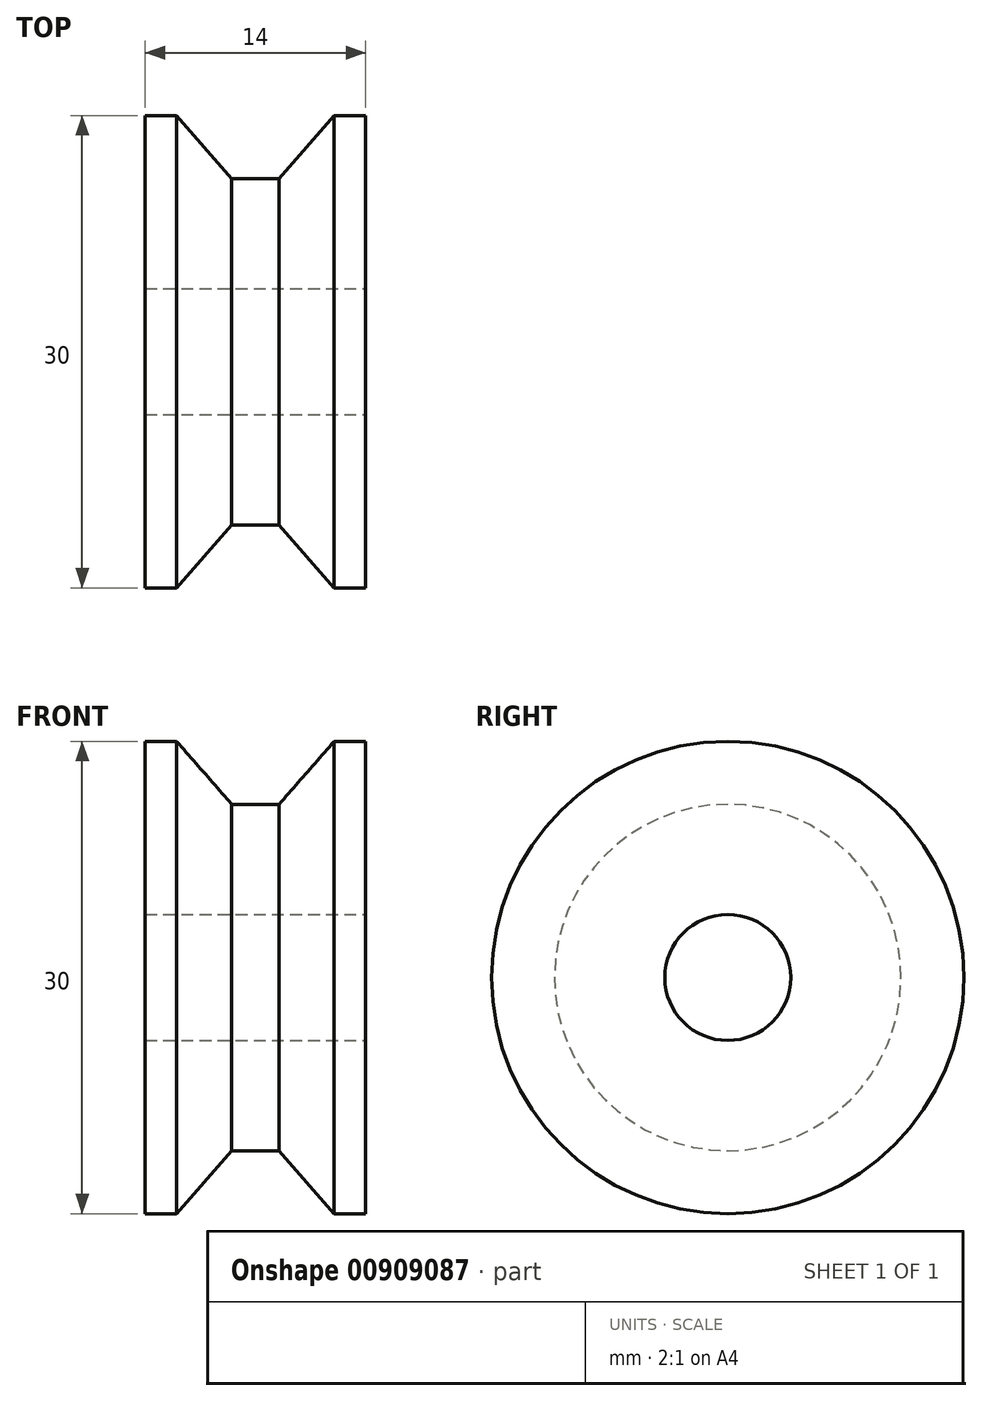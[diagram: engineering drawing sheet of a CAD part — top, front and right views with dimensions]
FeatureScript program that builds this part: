
annotation { "Feature Type Name" : "Feature", "Feature Type Description" : "" }
export const myFeature = defineFeature(function(context is Context, id is Id, definition is map)
    precondition{}
    {
        {
            var Q0;
            Q0=qCreatedBy(makeId("Front.planeOp"),FACE);
            var sketch = newSketch(context, id + "F0", { "sketchPlane" : qUnion([Q0])});
            skLineSegment(sketch, "E0", {"start": v(0, 0) * mm, "end": v(-7, 0) * mm});
            skLineSegment(sketch, "E1", {"start": v(-7, 0) * mm, "end": v(-7, 15) * mm});
            skLineSegment(sketch, "E2", {"start": v(-7, 15) * mm, "end": v(-5, 15) * mm});
            skLineSegment(sketch, "E3", {"start": v(-5, 15) * mm, "end": v(-1.5, 11) * mm});
            skLineSegment(sketch, "E4", {"start": v(-1.5, 11) * mm, "end": v(0, 11) * mm});
            skLineSegment(sketch, "E5", {"start": v(0, 11) * mm, "end": v(0, 0) * mm});
            skLineSegment(sketch, "E6.MirrorCS", {"start": v(0, 0) * mm, "end": v(7, 0) * mm});
            skLineSegment(sketch, "E7.MirrorCS", {"start": v(7, 0) * mm, "end": v(7, 15) * mm});
            skLineSegment(sketch, "E8.MirrorCS", {"start": v(7, 15) * mm, "end": v(5, 15) * mm});
            skLineSegment(sketch, "E9.MirrorCS", {"start": v(5, 15) * mm, "end": v(1.5, 11) * mm});
            skLineSegment(sketch, "E10.MirrorCS", {"start": v(1.5, 11) * mm, "end": v(0, 11) * mm});
            skSolve(sketch);
        }
        {
            var Q0;
            Q0=qCreatedBy(makeId("Right.planeOp"),FACE);
            var sketch = newSketch(context, id + "F1", { "sketchPlane" : qUnion([Q0])});
            skCircle(sketch, "E11", {"center": v(0, 0) * mm, "radius": 4 * mm});
            skSolve(sketch);
        }
        {
            var Q0;
            Q0=makeQuery(id+"F0.imprint","IMPRINT",FACE,{"disambiguationData":[TD([[makeQuery(id+"F0.imprint","IMPRINT",EDGE,{"derivedFrom":sQuery(id+"F0.wireOp",EDGE,"E5")}),1.0]])]});
            var Q1;
            Q1=makeQuery(id+"F0.imprint","IMPRINT",FACE,{"disambiguationData":[TD([[makeQuery(id+"F0.imprint","IMPRINT",EDGE,{"derivedFrom":sQuery(id+"F0.wireOp",EDGE,"E0")}),-1.0]])]});
            var Q2;
            Q2=sQuery(id+"F1.wireOp",EDGE,"E11");
            revolve(context, id + "F2", {"surfaceOperationType" : NewSurfaceOperationType.NEW, "entities" : qUnion([Q0, Q1]), "axis" : qUnion([Q2]), "revolveType" : RevolveType.FULL});
        }
        {
            var Q0;
            Q0=qSketchRegion(id+"F1",true);
            extrude(context, id + "F3", {"entities" : qUnion([Q0]), "operationType" : NewBodyOperationType.REMOVE, "endBound" : BoundingType.SYMMETRIC, "oppositeDirection" : true, "depth" : 25 * mm, "offsetDistance" : 25 * mm});
        }
    });
